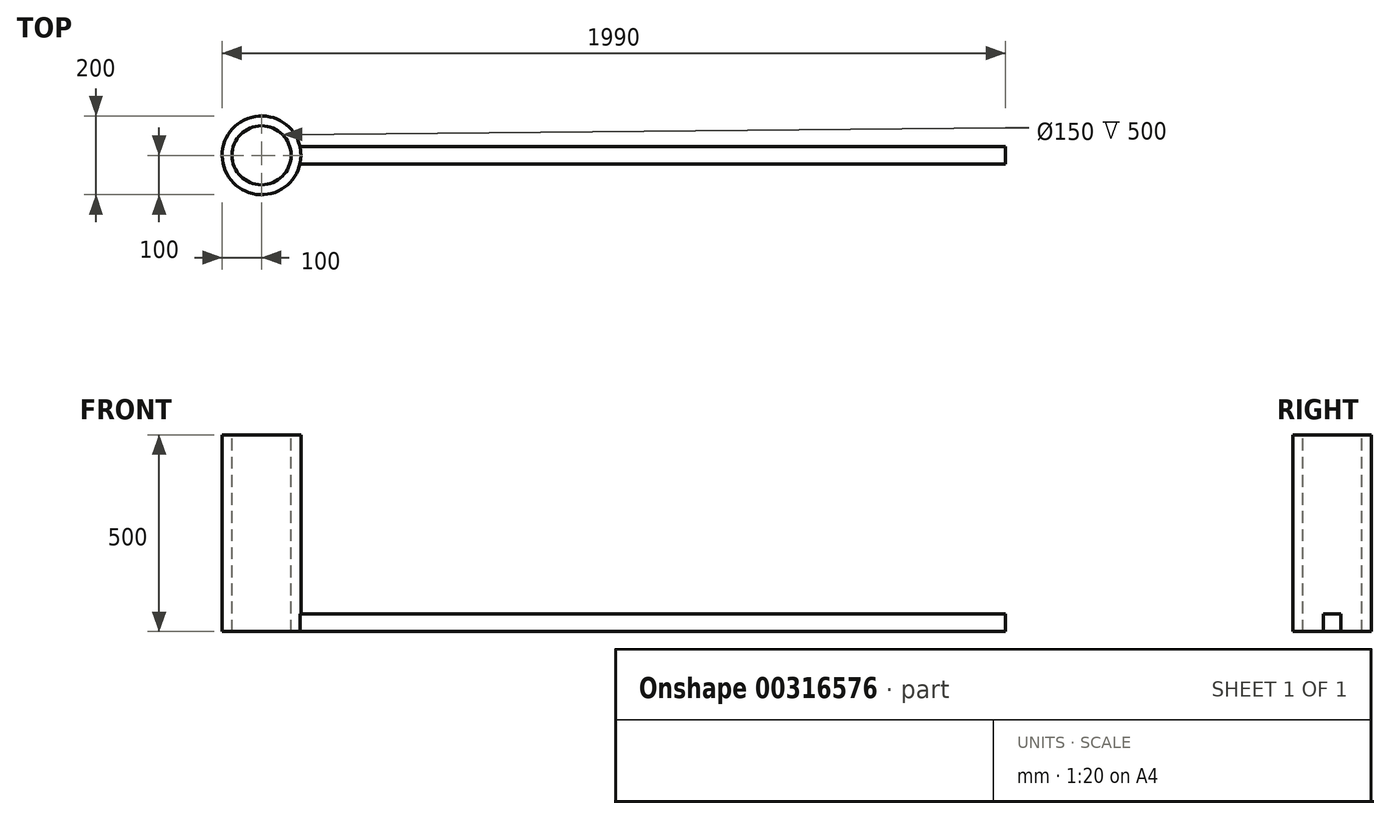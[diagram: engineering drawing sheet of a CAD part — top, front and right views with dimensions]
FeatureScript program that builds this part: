
annotation { "Feature Type Name" : "Feature", "Feature Type Description" : "" }
export const myFeature = defineFeature(function(context is Context, id is Id, definition is map)
    precondition{}
    {
        {
            var Q0;
            Q0=qCreatedBy(makeId("Top.planeOp"),FACE);
            var sketch = newSketch(context, id + "F0", { "sketchPlane" : qUnion([Q0])});
            skCircle(sketch, "E0", {"center": v(0, 0) * mm, "radius": 100 * mm});
            skSolve(sketch);
        }
        {
            var Q0;
            Q0=makeQuery(id+"F0.imprint","IMPRINT",FACE,{"disambiguationData":[TD([[makeQuery(id+"F0.imprint","IMPRINT",EDGE,{"derivedFrom":sQuery(id+"F0.wireOp",EDGE,"E0")}),1.0]])]});
            extrude(context, id + "F1", {"entities" : qUnion([Q0]), "depth" : 500 * mm});
        }
        {
            var Q0;
            Q0=makeQuery(id+"F1.opExtrude","CAP_FACE",FACE,{"disambiguationData":[OSD([sQuery(id+"F0.wireOp",EDGE,"E0")])],"isStart":false});
            var sketch = newSketch(context, id + "F2", { "sketchPlane" : qUnion([Q0])});
            skCircle(sketch, "E1", {"center": v(0, 0) * mm, "radius": 75 * mm});
            skSolve(sketch);
        }
        {
            var Q0;
            Q0=makeQuery(id+"F2.imprint","IMPRINT",FACE,{"disambiguationData":[TD([[makeQuery(id+"F2.imprint","IMPRINT",EDGE,{"derivedFrom":sQuery(id+"F2.wireOp",EDGE,"E1")}),1.0]])]});
            extrude(context, id + "F3", {"entities" : qUnion([Q0]), "operationType" : NewBodyOperationType.REMOVE, "endBound" : BoundingType.THROUGH_ALL, "oppositeDirection" : true, "depth" : 25 * mm});
        }
        {
            var Q0;
            Q0=qCreatedBy(makeId("Right.planeOp"),FACE);
            var sketch = newSketch(context, id + "F4", { "sketchPlane" : qUnion([Q0])});
            skLineSegment(sketch, "E2", {"start": v(-100, 0) * mm, "end": v(-100, 500) * mm});
            skLineSegment(sketch, "E3", {"start": v(100, 500) * mm, "end": v(100, 0) * mm});
            skLineSegment(sketch, "E4.bottom", {"start": v(22.5, 0) * mm, "end": v(-22.5, 0) * mm});
            skLineSegment(sketch, "E4.top", {"start": v(22.5, 45) * mm, "end": v(-22.5, 45) * mm});
            skLineSegment(sketch, "E4.left", {"start": v(22.5, 0) * mm, "end": v(22.5, 45) * mm});
            skLineSegment(sketch, "E4.right", {"start": v(-22.5, 0) * mm, "end": v(-22.5, 45) * mm});
            skPoint(sketch, "E4.middle", {"position": v(0, 22.5) * mm});
            skSolve(sketch);
        }
        {
            var Q0;
            Q0=makeQuery(id+"F4.imprint","IMPRINT",FACE,{"disambiguationData":[TD([[makeQuery(id+"F4.imprint","IMPRINT",EDGE,{"derivedFrom":sQuery(id+"F4.wireOp",EDGE,"E4.bottom")}),-1.0]])]});
            extrude(context, id + "F5", {"entities" : qUnion([Q0]), "operationType" : NewBodyOperationType.ADD, "depth" : 1890 * mm});
        }
        {
            var Q0;
            Q0=makeQuery(id+"F5.boolean.opBoolean","MERGE",FACE,{"derivedFrom":[makeQuery(id+"F1.opExtrude","CAP_FACE",FACE,{"disambiguationData":[OSD([sQuery(id+"F0.wireOp",EDGE,"E0")])],"isStart":true}),makeQuery(id+"F5.opExtrude","SWEPT_FACE",FACE,{"disambiguationData":[OSD([sQuery(id+"F4.wireOp",EDGE,"E4.bottom")])]})]});
            var sketch = newSketch(context, id + "F6", { "sketchPlane" : qUnion([Q0])});
            skCircle(sketch, "E5", {"center": v(0, 0) * mm, "radius": 75 * mm});
            skSolve(sketch);
        }
        {
            var Q0;
            Q0=makeQuery(id+"F6.imprint","IMPRINT",FACE,{"disambiguationData":[TD([[makeQuery(id+"F6.imprint","IMPRINT",EDGE,{"disambiguationData":[OD(1.0)],"derivedFrom":sQuery(id+"F6.wireOp",EDGE,"E5")}),1.0]])]});
            extrude(context, id + "F7", {"entities" : qUnion([Q0]), "operationType" : NewBodyOperationType.REMOVE, "endBound" : BoundingType.THROUGH_ALL, "oppositeDirection" : true, "depth" : 25 * mm});
        }
    });
